# Revit family: Food-Service-Equipment_Oscartek_Pozzetti_PS12
name_source: partatom
category: Specialty Equipment
units: mm (PartAtom-declared; Revit-internal decimal feet)

## family parameters
Always vertical = Yes
Classification Number = 23.40.40.11.17
Cut with Voids When Loaded = No
Enable Cutting in Views = No
Maintain Annotation Orientation = No
Part Type = Normal
Room Calculation Point = No
Round Connector Dimension = Use Diameter
Shared = No
Work Plane-Based = No

## types (1)
- Food-Service-Equipment_Oscartek_Pozzetti_PS12
    Apparent Power = 0 VA
    BTUH = 0.0 Btu/h
    Building Codes = https://www.arcat.com
    CSI MasterFormat = 11 41 13
    Conn Conduit = Yes
    Construction Details = http://www.oscartek.com
    Cycle = 60 Hz
    Default Elevation = 0 "
    Depth = 25.79 "
    Description = POZZETTI WITH STORAGE (SELF CONTAINED)
    Elec Conn Connection Height = 0 "
    Elec Conn RI Height = 0 "
    FL Amps = 15 A
    Foodservice Equipment Identifier = Yes
    Green Building-LEED = https://www.arcat.com
    Height = 36.65 "
    Identify Quantity as Lot = Yes
    Indirect Waste Connection Height = 0 "
    Indirect Waste Flow = 0 GPM
    Indirect Waste Size = 1"
    Installation-Fabrication = http://www.oscartek.com
    Length = 98.43 "
    Manufacturer = OSCARTEK
    Manufacturer Fax = 650-342-7400
    Manufacturer Website = http://www.oscartek.com
    Max Overcurrent Protection = 0 A
    Min Ckt Ampacity = 0 A
    Model = POZZETTI PS12
    Number of Poles = 1
    Phase = 1
    Product Data = http://www.oscartek.com
    Refrigerant Type = R404A
    Refrigerant Volume = 0.00 kip
    Revision = R1_2018-10
    Sales Information = http://www.oscartek.com
    Specification = https://www.arcat.com
    Test Data = http://www.oscartek.com
    Type Comments = As Specified
    URL = www.oscartek.com
    URL Cutsheet = www.oscartek.com
    Volts = 115 V
    Waste Water Discharge Temperature = 0 °F
    Watts = 1725 W
    Weight in Pounds = 820

## geometry (parser evidence)
native form markers: Blend x12, Sweep x8
no freeform markers — native parametric forms only
